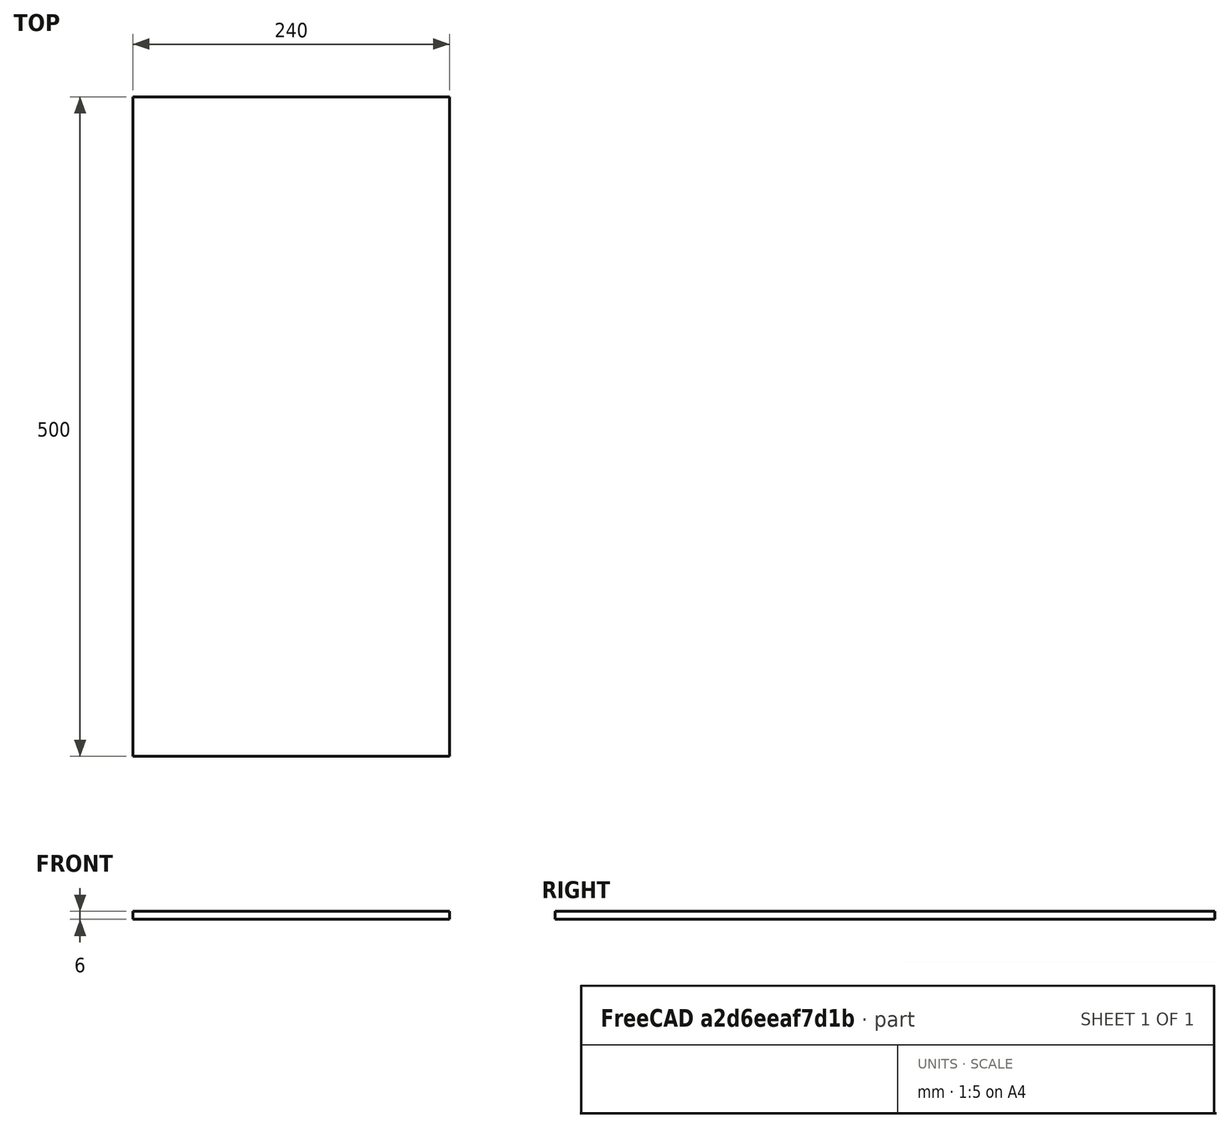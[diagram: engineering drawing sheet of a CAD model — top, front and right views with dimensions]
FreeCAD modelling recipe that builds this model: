
FCSTD DOCUMENT  (FreeCAD 0.18R4 (GitTag))
Label: Gabinete_top
License: All rights reserved
LicenseURL: http://en.wikipedia.org/wiki/All_rights_reserved
objects: Sketcher::SketchObject×1, PartDesign::Pad×1, PartDesign::Body×1
note: 4 computed .brp shape members not serialized (recipe doc carries the construction recipe); baked Part::Feature solids carry a one-line shape summary decoded from their .brp

FEATURE [Sketcher::SketchObject] Sketch
  MapMode = 5
  Support = -> [XY_Plane]
  sketch-geometry (4):
    g0: LineSegment StartX=0 StartY=0 StartZ=0 EndX=240 EndY=0 EndZ=0
    g1: LineSegment StartX=240 StartY=0 StartZ=0 EndX=240 EndY=500 EndZ=0
    g2: LineSegment StartX=240 StartY=500 StartZ=0 EndX=0 EndY=500 EndZ=0
    g3: LineSegment StartX=0 StartY=500 StartZ=0 EndX=0 EndY=0 EndZ=0
  constraints (11):
    c: Coincident(g0,g1)
    c: Coincident(g1,g2)
    c: Coincident(g2,g3)
    c: Coincident(g3,g0)
    c: Horizontal(g0)
    c: Horizontal(g2)
    c: Vertical(g1)
    c: Vertical(g3)
    c: DistanceX(g0,g0) = 240
    c: DistanceY(g3,g3) = 500
    c: Coincident(g0,g-1)
FEATURE [PartDesign::Pad] Pad
  Length = 6
  Length2 = 100
  Profile = -> Sketch
  Type = 0
FEATURE [PartDesign::Body] Body
  Group = -> [Sketch,Pad]
  Origin = -> Origin
  Tip = -> Pad
